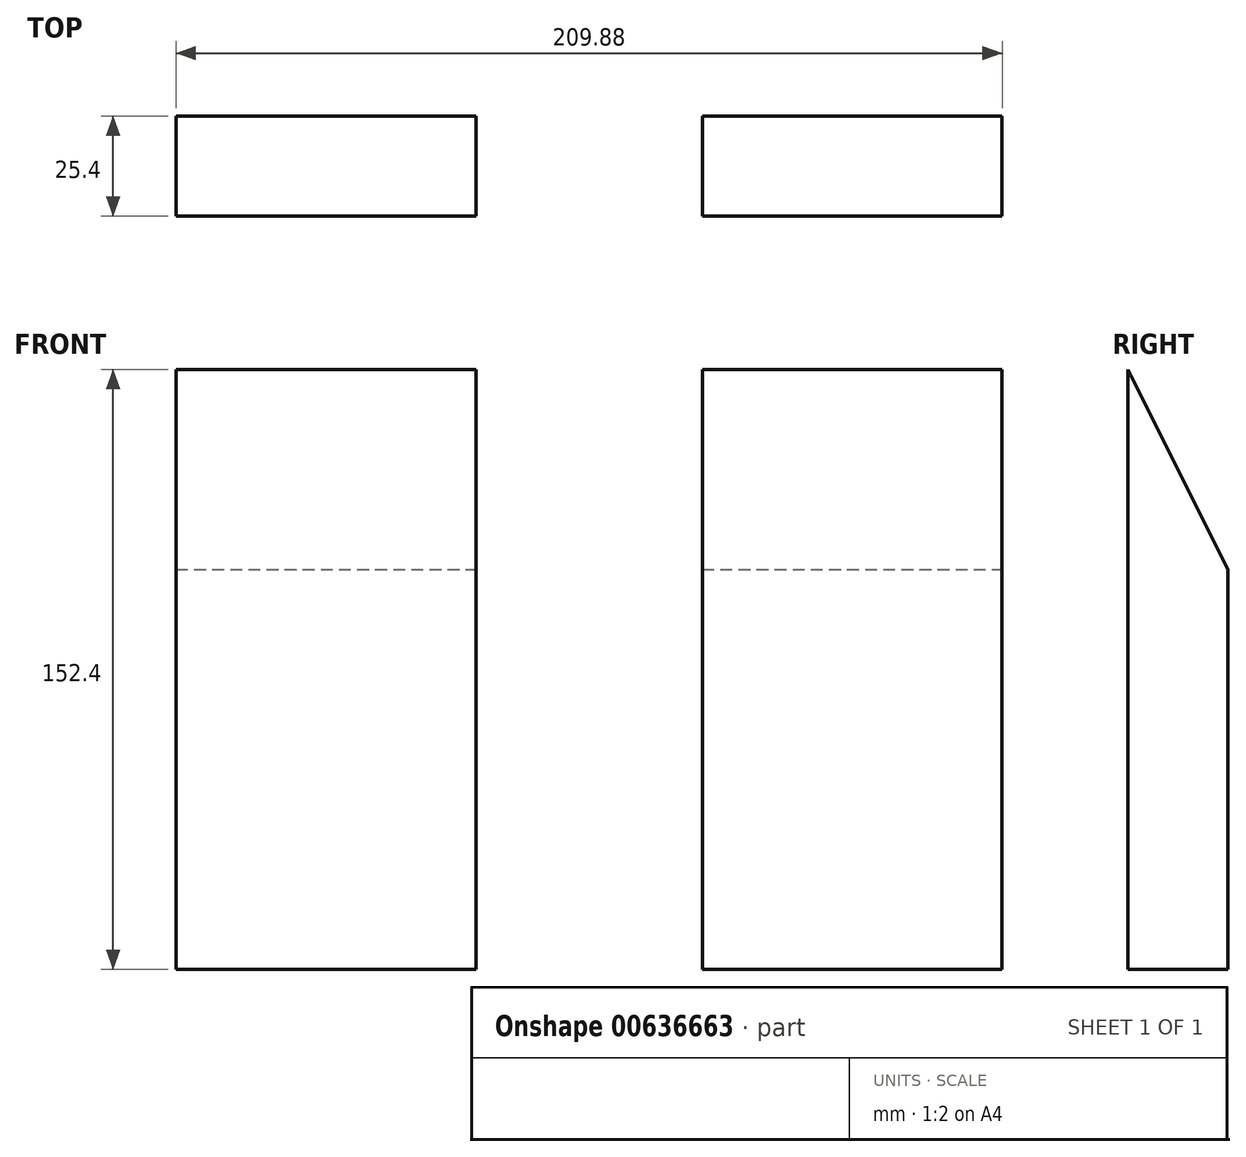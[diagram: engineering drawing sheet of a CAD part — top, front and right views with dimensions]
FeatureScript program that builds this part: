
annotation { "Feature Type Name" : "Feature", "Feature Type Description" : "" }
export const myFeature = defineFeature(function(context is Context, id is Id, definition is map)
    precondition{}
    {
        {
            var Q0;
            Q0=qCreatedBy(makeId("Front.planeOp"),FACE);
            var sketch = newSketch(context, id + "F0", { "sketchPlane" : qUnion([Q0])});
            skLineSegment(sketch, "E0.bottom", {"start": v(-76.87, 86.75) * mm, "end": v(-0.67, 86.75) * mm});
            skLineSegment(sketch, "E0.top", {"start": v(-76.87, -65.65) * mm, "end": v(-0.67, -65.65) * mm});
            skLineSegment(sketch, "E0.left", {"start": v(-76.87, 86.75) * mm, "end": v(-76.87, -65.65) * mm});
            skLineSegment(sketch, "E0.right", {"start": v(-0.67, 86.75) * mm, "end": v(-0.67, -65.65) * mm});
            skLineSegment(sketch, "E1.bottom", {"start": v(56.8, 86.75) * mm, "end": v(133, 86.75) * mm});
            skLineSegment(sketch, "E1.top", {"start": v(56.8, -65.65) * mm, "end": v(133, -65.65) * mm});
            skLineSegment(sketch, "E1.left", {"start": v(56.8, 86.75) * mm, "end": v(56.8, -65.65) * mm});
            skLineSegment(sketch, "E1.right", {"start": v(133, 86.75) * mm, "end": v(133, -65.65) * mm});
            skSolve(sketch);
        }
        {
            var Q0;
            Q0=makeQuery(id+"F0.imprint","IMPRINT",FACE,{"disambiguationData":[TD([[makeQuery(id+"F0.imprint","IMPRINT",EDGE,{"derivedFrom":sQuery(id+"F0.wireOp",EDGE,"E0.bottom")}),-1.0]])]});
            extrude(context, id + "F1", {"entities" : qUnion([Q0]), "depth" : 25.4 * mm, "offsetDistance" : 25.4 * mm});
        }
        {
            var Q0;
            Q0=makeQuery(id+"F0.imprint","IMPRINT",FACE,{"disambiguationData":[TD([[makeQuery(id+"F0.imprint","IMPRINT",EDGE,{"derivedFrom":sQuery(id+"F0.wireOp",EDGE,"E1.bottom")}),-1.0]])]});
            extrude(context, id + "F2", {"entities" : qUnion([Q0]), "depth" : 25.4 * mm, "offsetDistance" : 25.4 * mm});
        }
        {
            var Q0;
            Q0=makeQuery(id+"F2.opExtrude","SWEPT_FACE",FACE,{"disambiguationData":[OSD([sQuery(id+"F0.wireOp",EDGE,"E1.right")])]});
            var sketch = newSketch(context, id + "F3", { "sketchPlane" : qUnion([Q0])});
            skLineSegment(sketch, "E2", {"start": v(-25.4, 86.75) * mm, "end": v(0, 35.95) * mm});
            skSolve(sketch);
        }
        {
            var Q0;
            {var subQ0=sQuery(id+"F3.wireOp",EDGE,"E2");Q0=makeQuery(id+"F3.imprint","IMPRINT",FACE,{"disambiguationData":[TD([[makeQuery(id+"F3.imprint","IMPRINT",EDGE,{"derivedFrom":subQ0}),1.0]])]});}
            extrude(context, id + "F4", {"entities" : qUnion([Q0]), "operationType" : NewBodyOperationType.REMOVE, "oppositeDirection" : true, "depth" : 76.2 * mm, "offsetDistance" : 25.4 * mm});
        }
        {
            var Q0;
            Q0=makeQuery(id+"F1.opExtrude","SWEPT_FACE",FACE,{"disambiguationData":[OSD([sQuery(id+"F0.wireOp",EDGE,"E0.right")])]});
            var sketch = newSketch(context, id + "F5", { "sketchPlane" : qUnion([Q0])});
            skLineSegment(sketch, "E3", {"start": v(-25.4, 86.75) * mm, "end": v(0, 35.95) * mm});
            skSolve(sketch);
        }
        {
            var Q0;
            {var subQ0=sQuery(id+"F5.wireOp",EDGE,"E3");Q0=makeQuery(id+"F5.imprint","IMPRINT",FACE,{"disambiguationData":[TD([[makeQuery(id+"F5.imprint","IMPRINT",EDGE,{"derivedFrom":subQ0}),1.0]])]});}
            extrude(context, id + "F6", {"entities" : qUnion([Q0]), "operationType" : NewBodyOperationType.REMOVE, "oppositeDirection" : true, "depth" : 76.2 * mm, "offsetDistance" : 25.4 * mm});
        }
    });
